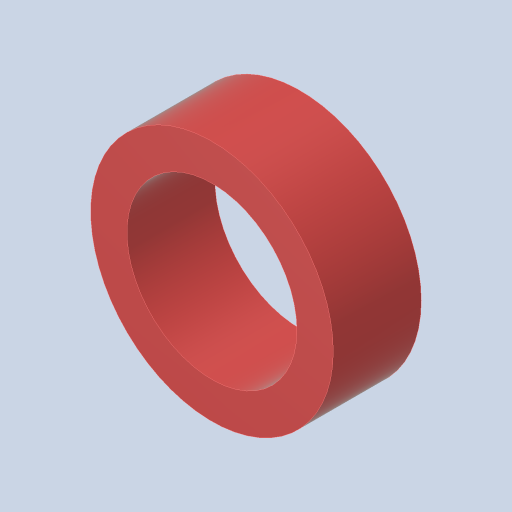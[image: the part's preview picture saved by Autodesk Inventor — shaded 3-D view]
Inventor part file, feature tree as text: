
AUTODESK INVENTOR PART (.ipt)
format: ipt  version: 2023.4 (Build 274418000, 418)  size: 121,344 bytes
history: native  units: in
note: dims shown in document units (in); Inventor stores cm internally (conversion verified against a paired STEP export)
features: extrude x1, sketch x1
ambient origin geometry x8: Origin, YZ Plane, XZ Plane, XY Plane, X Axis, Y Axis, Z Axis, Center Point
bodies: Solid1 (feature_tree)
feature tree (2):
  extrude  "Extrusion1"  Depth=0.303in
  sketch  "Sketch1"  dims[d0=0.585in d1=0.125in d2=0.303in d3=0.0in]
